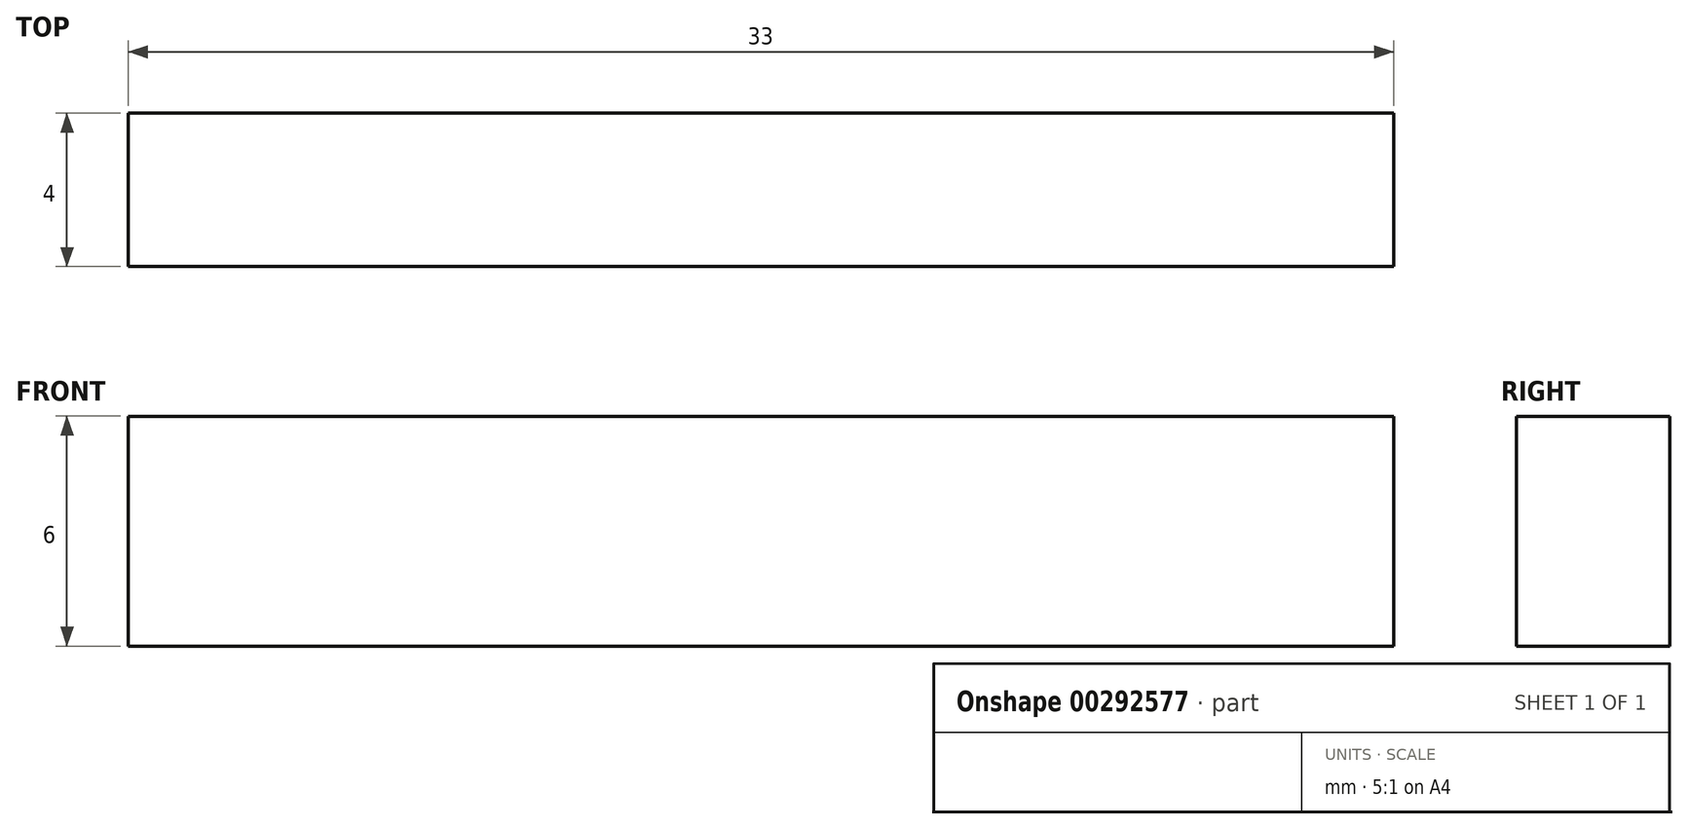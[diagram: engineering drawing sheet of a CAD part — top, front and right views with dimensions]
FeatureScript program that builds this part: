
annotation { "Feature Type Name" : "Feature", "Feature Type Description" : "" }
export const myFeature = defineFeature(function(context is Context, id is Id, definition is map)
    precondition{}
    {
        {
            var Q0;
            Q0=qCreatedBy(makeId("Front.planeOp"),FACE);
            var sketch = newSketch(context, id + "F0", { "sketchPlane" : qUnion([Q0])});
            skLineSegment(sketch, "E0", {"start": v(-14.88, -2.37) * mm, "end": v(18.12, -2.37) * mm});
            skLineSegment(sketch, "E1", {"start": v(18.12, -2.37) * mm, "end": v(18.12, -8.37) * mm});
            skLineSegment(sketch, "E2", {"start": v(18.12, -8.37) * mm, "end": v(-14.88, -8.37) * mm});
            skLineSegment(sketch, "E3", {"start": v(-14.88, -8.37) * mm, "end": v(-14.88, -2.37) * mm});
            skSolve(sketch);
        }
        {
            var Q0;
            Q0 = qSketchRegion(id + "F0", true);
            extrude(context, id + "F1", {"entities" : qUnion([Q0]), "depth" : 4 * mm});
        }
    });
